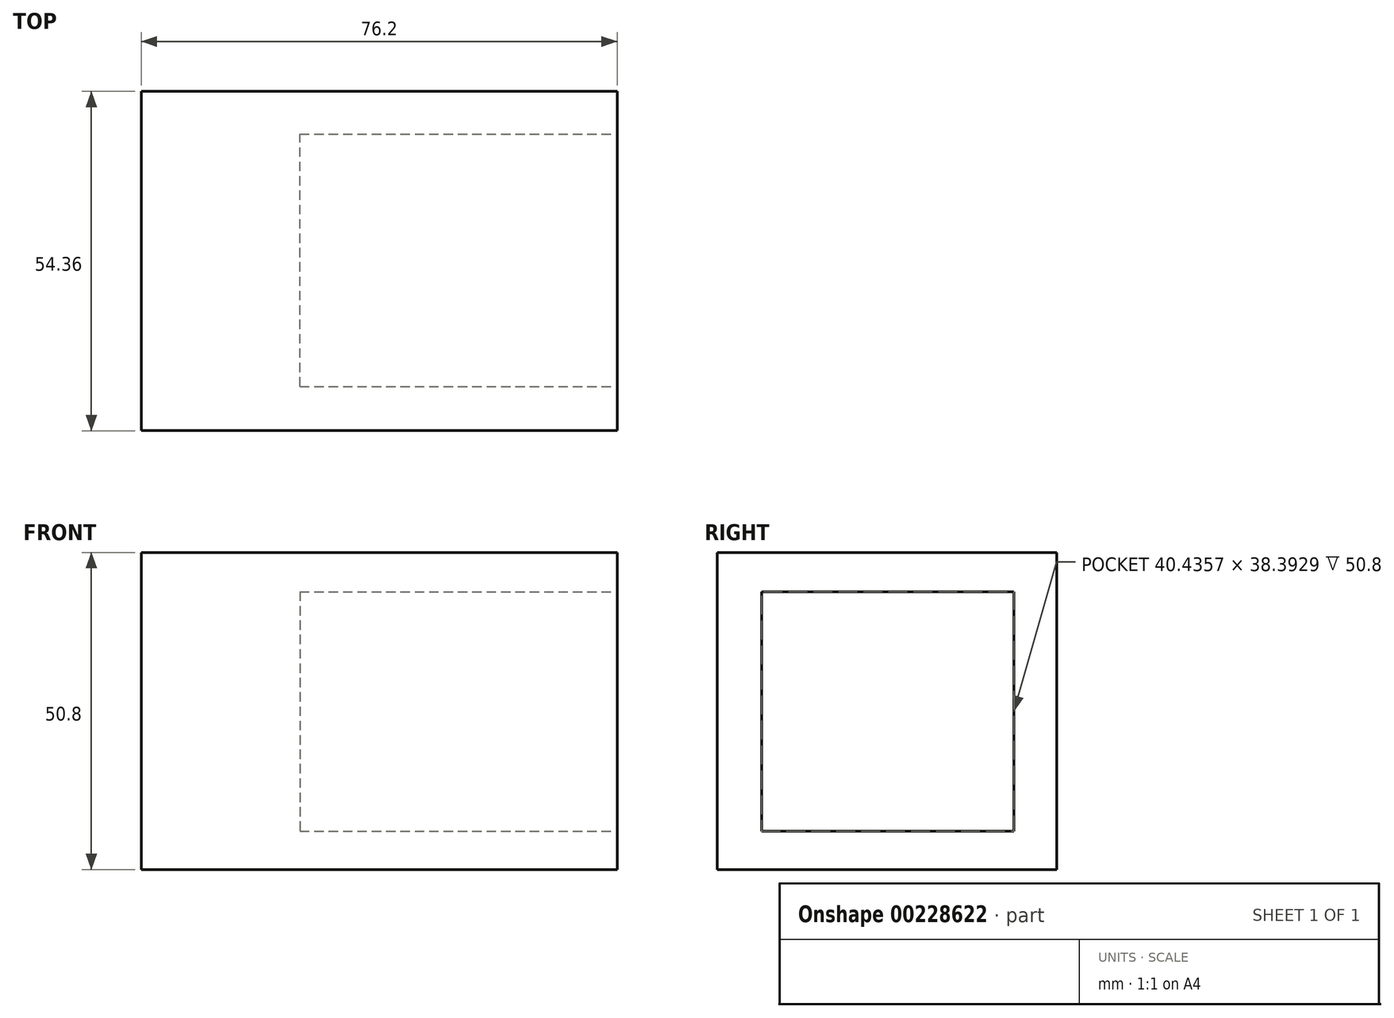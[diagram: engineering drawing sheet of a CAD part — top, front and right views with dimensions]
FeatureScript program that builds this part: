
annotation { "Feature Type Name" : "Feature", "Feature Type Description" : "" }
export const myFeature = defineFeature(function(context is Context, id is Id, definition is map)
    precondition{}
    {
        {
            var Q0;
            Q0=qCreatedBy(makeId("Top.planeOp"),FACE);
            var sketch = newSketch(context, id + "F0", { "sketchPlane" : qUnion([Q0])});
            skLineSegment(sketch, "E0.bottom", {"start": v(38.1, -27.18) * mm, "end": v(-38.1, -27.18) * mm});
            skLineSegment(sketch, "E0.top", {"start": v(38.1, 27.18) * mm, "end": v(-38.1, 27.18) * mm});
            skLineSegment(sketch, "E0.left", {"start": v(38.1, -27.18) * mm, "end": v(38.1, 27.18) * mm});
            skLineSegment(sketch, "E0.right", {"start": v(-38.1, -27.18) * mm, "end": v(-38.1, 27.18) * mm});
            skPoint(sketch, "E0.middle", {"position": v(0, 0) * mm});
            skSolve(sketch);
        }
        {
            var Q0;
            Q0 = qSketchRegion(id + "F0", true);
            extrude(context, id + "F1", {"entities" : qUnion([Q0]), "depth" : 50.8 * mm});
        }
        {
            var Q0;
            Q0=makeQuery(id+"F1.opExtrude","SWEPT_FACE",FACE,{"disambiguationData":[OSD([sQuery(id+"F0.wireOp",EDGE,"E0.left")])]});
            var sketch = newSketch(context, id + "F2", { "sketchPlane" : qUnion([Q0])});
            skLineSegment(sketch, "E1.bottom", {"start": v(-20.09, 44.5) * mm, "end": v(20.35, 44.5) * mm});
            skLineSegment(sketch, "E1.top", {"start": v(-20.09, 6.1) * mm, "end": v(20.35, 6.1) * mm});
            skLineSegment(sketch, "E1.left", {"start": v(-20.09, 44.5) * mm, "end": v(-20.09, 6.1) * mm});
            skLineSegment(sketch, "E1.right", {"start": v(20.35, 44.5) * mm, "end": v(20.35, 6.1) * mm});
            skSolve(sketch);
        }
        {
            var Q0;
            Q0=makeQuery(id+"F2.imprint","IMPRINT",FACE,{"disambiguationData":[TD([[makeQuery(id+"F2.imprint","IMPRINT",EDGE,{"derivedFrom":sQuery(id+"F2.wireOp",EDGE,"E1.bottom")}),-1.0]])]});
            extrude(context, id + "F3", {"entities" : qUnion([Q0]), "operationType" : NewBodyOperationType.REMOVE, "oppositeDirection" : true, "depth" : 50.8 * mm});
        }
    });
